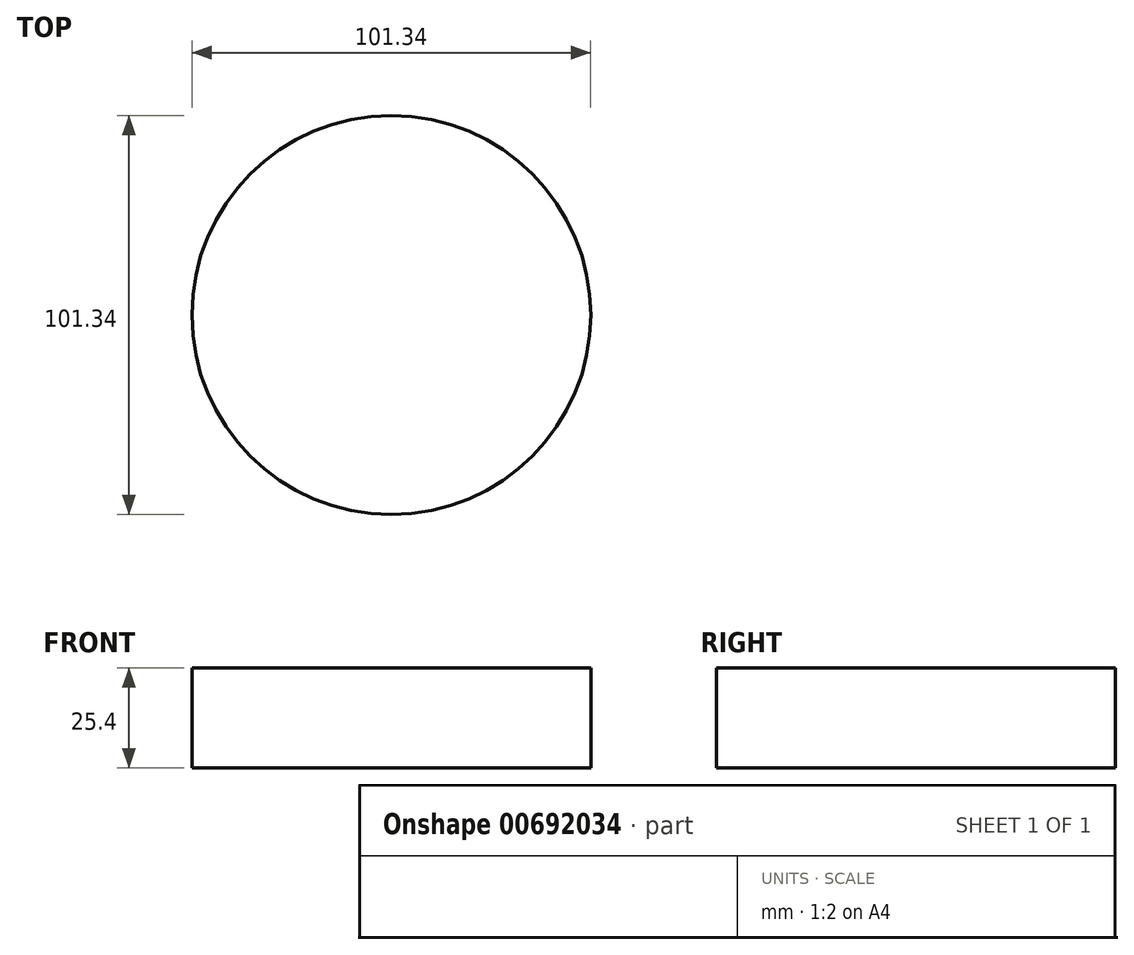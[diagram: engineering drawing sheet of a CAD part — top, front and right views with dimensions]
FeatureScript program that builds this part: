
annotation { "Feature Type Name" : "Feature", "Feature Type Description" : "" }
export const myFeature = defineFeature(function(context is Context, id is Id, definition is map)
    precondition{}
    {
        {
            var Q0;
            Q0=qCreatedBy(makeId("Top.planeOp"),FACE);
            var sketch = newSketch(context, id + "F0", { "sketchPlane" : qUnion([Q0])});
            skCircle(sketch, "E0", {"center": v(0, 0) * mm, "radius": 50.67 * mm});
            skSolve(sketch);
        }
        {
            var Q0;
            Q0 = qSketchRegion(id + "F0", true);
            extrude(context, id + "F1", {"entities" : qUnion([Q0]), "depth" : 25.4 * mm, "offsetDistance" : 25.4 * mm});
        }
    });
